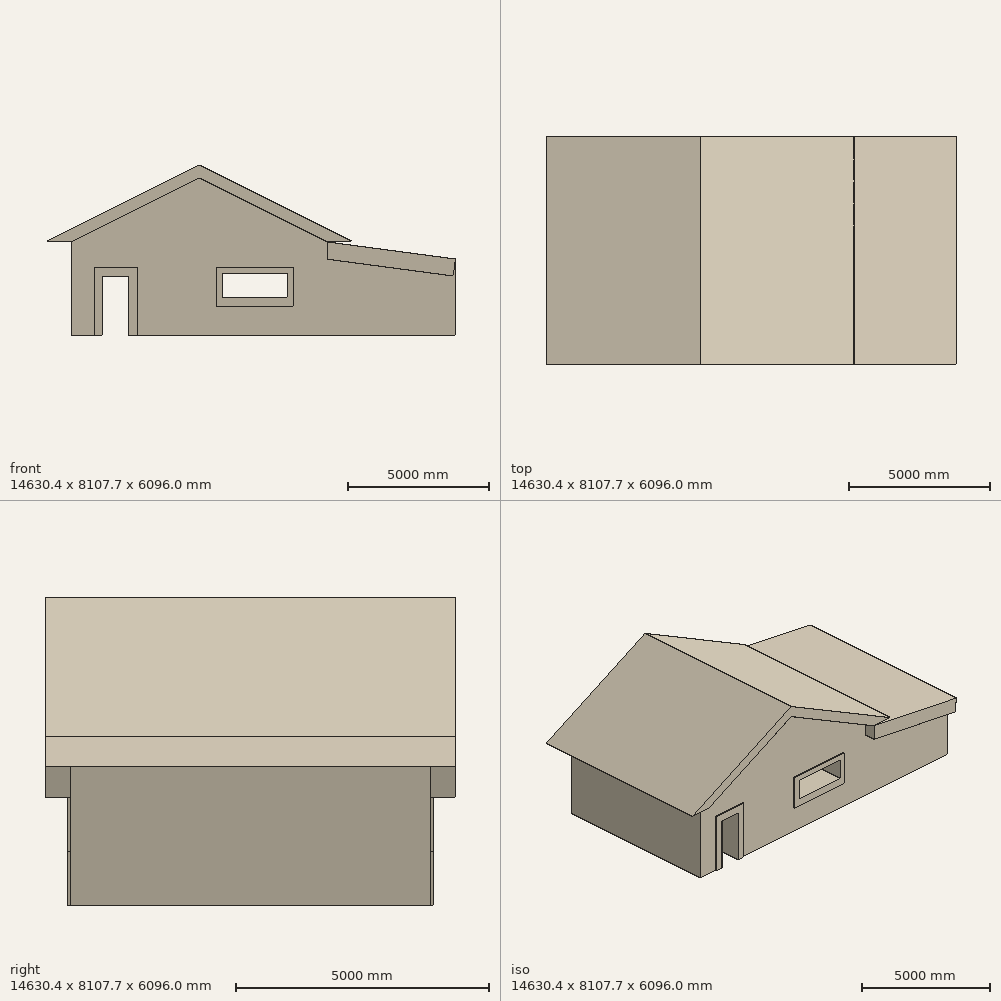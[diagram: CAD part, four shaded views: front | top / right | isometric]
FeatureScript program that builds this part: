
annotation { "Feature Type Name" : "Feature", "Feature Type Description" : "" }
export const myFeature = defineFeature(function(context is Context, id is Id, definition is map)
    precondition{}
    {
        {
            var Q0;
            Q0=qCreatedBy(makeId("Front.planeOp"),FACE);
            var sketch = newSketch(context, id + "F0", { "sketchPlane" : qUnion([Q0])});
            skLineSegment(sketch, "E0", {"start": v(0, 0) * mm, "end": v(-9144, 0) * mm});
            skLineSegment(sketch, "E1", {"start": v(-9144, 0) * mm, "end": v(-9144, 609.6) * mm});
            skLineSegment(sketch, "E2", {"start": v(0, 0) * mm, "end": v(0, 609.6) * mm});
            skLineSegment(sketch, "E3", {"start": v(0, 609.6) * mm, "end": v(-9144, 609.6) * mm});
            skLineSegment(sketch, "E4", {"start": v(-9144, 609.6) * mm, "end": v(-9144, 3962.4) * mm});
            skLineSegment(sketch, "E5", {"start": v(0, 609.6) * mm, "end": v(0, 3962.4) * mm});
            skLineSegment(sketch, "E6", {"start": v(-9144, 3962.4) * mm, "end": v(0, 3962.4) * mm});
            skLineSegment(sketch, "E7", {"start": v(-9144, 3962.4) * mm, "end": v(-10058.4, 3962.4) * mm});
            skLineSegment(sketch, "E8", {"start": v(0, 3962.4) * mm, "end": v(914.4, 3962.4) * mm});
            skLineSegment(sketch, "E9", {"start": v(-4572, 3962.4) * mm, "end": v(-4572, 6248.4) * mm});
            skLineSegment(sketch, "E10", {"start": v(-4572, 6248.4) * mm, "end": v(-4572, 6705.6) * mm});
            skLineSegment(sketch, "E11", {"start": v(-9144, 3962.4) * mm, "end": v(-4572, 6248.4) * mm});
            skLineSegment(sketch, "E12", {"start": v(-4572, 6248.4) * mm, "end": v(0, 3962.4) * mm});
            skLineSegment(sketch, "E13", {"start": v(914.4, 3962.4) * mm, "end": v(-4572, 6705.6) * mm});
            skLineSegment(sketch, "E14", {"start": v(-4572, 6705.6) * mm, "end": v(-10058.4, 3962.4) * mm});
            skLineSegment(sketch, "E15", {"start": v(0, 0) * mm, "end": v(4572, 0) * mm});
            skLineSegment(sketch, "E16", {"start": v(4572, 0) * mm, "end": v(4572, 609.6) * mm});
            skLineSegment(sketch, "E17", {"start": v(4572, 609.6) * mm, "end": v(0, 609.6) * mm});
            skLineSegment(sketch, "E18", {"start": v(4572, 609.6) * mm, "end": v(4572, 3352.8) * mm});
            skLineSegment(sketch, "E19", {"start": v(4572, 3352.8) * mm, "end": v(0, 3962.4) * mm});
            skLineSegment(sketch, "E20", {"start": v(4572, 3352.8) * mm, "end": v(4491.43, 2748.55) * mm});
            skLineSegment(sketch, "E21", {"start": v(4491.43, 2748.55) * mm, "end": v(0, 3347.4) * mm});
            skPoint(sketch, "E22.endSnap0", {"position": v(-9144, 2286) * mm});
            skLineSegment(sketch, "E23", {"start": v(-8006.82, 609.6) * mm, "end": v(-8006.82, 2743.2) * mm});
            skLineSegment(sketch, "E24", {"start": v(-8006.82, 2743.2) * mm, "end": v(-7092.42, 2743.2) * mm});
            skLineSegment(sketch, "E25", {"start": v(-7092.42, 2743.2) * mm, "end": v(-7092.42, 609.6) * mm});
            skLineSegment(sketch, "E26", {"start": v(-8006.82, 609.6) * mm, "end": v(-8311.62, 609.6) * mm});
            skLineSegment(sketch, "E27", {"start": v(-8311.62, 609.6) * mm, "end": v(-8311.62, 3048) * mm});
            skLineSegment(sketch, "E28", {"start": v(-7092.42, 609.6) * mm, "end": v(-6787.62, 609.6) * mm});
            skLineSegment(sketch, "E29", {"start": v(-6787.62, 609.6) * mm, "end": v(-6787.62, 3048) * mm});
            skLineSegment(sketch, "E30", {"start": v(-6787.62, 3048) * mm, "end": v(-8311.62, 3048) * mm});
            skLineSegment(sketch, "E31", {"start": v(-1219.2, 1676.4) * mm, "end": v(-1219.2, 3048) * mm});
            skLineSegment(sketch, "E32", {"start": v(-1219.2, 3048) * mm, "end": v(-3962.4, 3048) * mm});
            skLineSegment(sketch, "E33", {"start": v(-3962.4, 3048) * mm, "end": v(-3962.4, 1676.4) * mm});
            skLineSegment(sketch, "E34", {"start": v(-3734.28, 1984.45) * mm, "end": v(-3734.28, 2831.13) * mm});
            skLineSegment(sketch, "E35", {"start": v(-3734.28, 2831.13) * mm, "end": v(-1432.39, 2831.13) * mm});
            skLineSegment(sketch, "E36", {"start": v(-1432.39, 2831.13) * mm, "end": v(-1432.39, 1984.4) * mm});
            skLineSegment(sketch, "E37", {"start": v(-1432.39, 1984.4) * mm, "end": v(-3734.28, 1984.45) * mm});
            skPoint(sketch, "E38.endSnap0", {"position": v(-3734.28, 2407.8) * mm});
            skLineSegment(sketch, "E39", {"start": v(-3962.4, 1676.4) * mm, "end": v(-1219.2, 1676.4) * mm});
            skText(sketch, "E40", { "text": "matt.s", "fontName": "OpenSans-Regular.ttf"});
            skText(sketch, "E41", { "text": "matt.s", "fontName": "OpenSans-Regular.ttf"});
            const initialGuessF0  = {"E40": [-8.33915, -4.89846, 1, 0, 3.11618], "E41": [-7.84946, 0, 1, 0, 0.6096]};
            skSetInitialGuess(sketch, initialGuessF0);
            skSolve(sketch);
        }
        {
            var Q0;
            Q0=makeQuery(id+"F0.imprint","IMPRINT",FACE,{"disambiguationData":[TD([[makeQuery(id+"F0.imprint","IMPRINT",EDGE,{"derivedFrom":sQuery(id+"F0.wireOp",EDGE,"E7")}),-1.0]])]});
            var Q1;
            Q1=makeQuery(id+"F0.imprint","IMPRINT",FACE,{"disambiguationData":[TD([[makeQuery(id+"F0.imprint","IMPRINT",EDGE,{"derivedFrom":sQuery(id+"F0.wireOp",EDGE,"E8")}),1.0]])]});
            var Q2;
            {var subQ0=sQuery(id+"F0.wireOp",EDGE,"E19");Q2=makeQuery(id+"F0.imprint","IMPRINT",FACE,{"disambiguationData":[TD([[makeQuery(id+"F0.imprint","IMPRINT",EDGE,{"derivedFrom":subQ0}),1.0]])]});}
            extrude(context, id + "F1", {"entities" : qUnion([Q0, Q1, Q2]), "endBound" : BoundingType.SYMMETRIC, "depth" : 8107.68 * mm, "offsetDistance" : 30.48 * mm});
        }
        {
            var Q0;
            {var subQ2=sQuery(id+"F0.wireOp",EDGE,"E9");Q0=makeQuery(id+"F0.imprint","IMPRINT",FACE,{"disambiguationData":[TD([[makeQuery(id+"F0.imprint","IMPRINT",EDGE,{"derivedFrom":subQ2}),1.0]])]});}
            var Q1;
            {var subQ5=sQuery(id+"F0.wireOp",EDGE,"E4");Q1=makeQuery(id+"F0.imprint","IMPRINT",FACE,{"disambiguationData":[TD([[makeQuery(id+"F0.imprint","IMPRINT",EDGE,{"derivedFrom":subQ5}),-1.0]])]});}
            var Q2;
            {var subQ2=sQuery(id+"F0.wireOp",EDGE,"E9");Q2=makeQuery(id+"F0.imprint","IMPRINT",FACE,{"disambiguationData":[TD([[makeQuery(id+"F0.imprint","IMPRINT",EDGE,{"derivedFrom":subQ2}),-1.0]])]});}
            var Q3;
            {var subQ0=sQuery(id+"F0.wireOp",EDGE,"E17");Q3=makeQuery(id+"F0.imprint","IMPRINT",FACE,{"disambiguationData":[TD([[makeQuery(id+"F0.imprint","IMPRINT",EDGE,{"derivedFrom":subQ0}),-1.0]])]});}
            extrude(context, id + "F2", {"entities" : qUnion([Q0, Q1, Q2, Q3]), "endBound" : BoundingType.SYMMETRIC, "depth" : 7132.32 * mm, "offsetDistance" : 30.48 * mm});
        }
        {
            var Q0;
            Q0=makeQuery(id+"F0.imprint","IMPRINT",FACE,{"disambiguationData":[TD([[makeQuery(id+"F0.imprint","IMPRINT",EDGE,{"derivedFrom":sQuery(id+"F0.wireOp",EDGE,"E23")}),1.0]])]});
            var Q1;
            Q1=makeQuery(id+"F0.imprint","IMPRINT",FACE,{"disambiguationData":[TD([[makeQuery(id+"F0.imprint","IMPRINT",EDGE,{"derivedFrom":sQuery(id+"F0.wireOp",EDGE,"E31")}),1.0]])]});
            extrude(context, id + "F3", {"entities" : qUnion([Q0, Q1]), "operationType" : NewBodyOperationType.ADD, "endBound" : BoundingType.SYMMETRIC, "depth" : 7254.24 * mm, "offsetDistance" : 30.48 * mm});
        }
    });
